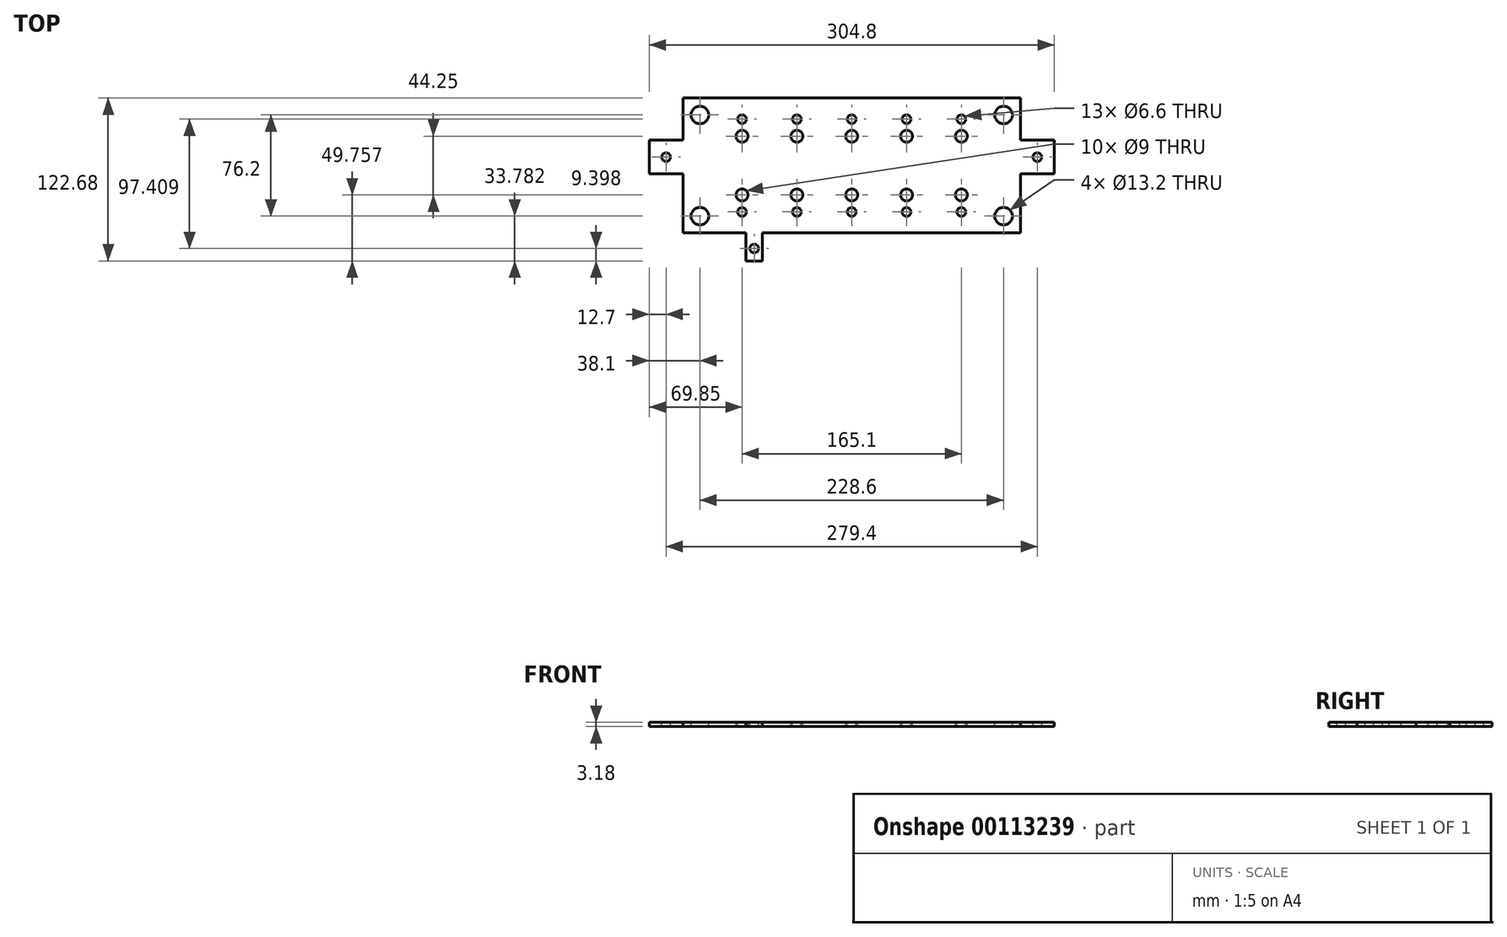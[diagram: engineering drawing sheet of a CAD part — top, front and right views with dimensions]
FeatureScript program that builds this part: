
annotation { "Feature Type Name" : "Feature", "Feature Type Description" : "" }
export const myFeature = defineFeature(function(context is Context, id is Id, definition is map)
    precondition{}
    {
        {
            var Q0;
            Q0=qCreatedBy(makeId("Top.planeOp"),FACE);
            var sketch = newSketch(context, id + "F0", { "sketchPlane" : qUnion([Q0])});
            skLineSegment(sketch, "E0.bottom", {"start": v(-102.08, 88.55) * mm, "end": v(177.32, 88.55) * mm});
            skLineSegment(sketch, "E0.top", {"start": v(-102.08, -13.05) * mm, "end": v(177.32, -13.05) * mm});
            skLineSegment(sketch, "E0.left", {"start": v(-102.08, 88.55) * mm, "end": v(-102.08, -13.05) * mm});
            skLineSegment(sketch, "E0.right", {"start": v(177.32, 88.55) * mm, "end": v(177.32, -13.05) * mm});
            skSolve(sketch);
        }
        {
            var Q0;
            Q0=makeQuery(id+"F0.imprint","IMPRINT",FACE,{"disambiguationData":[TD([[makeQuery(id+"F0.imprint","IMPRINT",EDGE,{"derivedFrom":sQuery(id+"F0.wireOp",EDGE,"E0.bottom")}),-1.0]])]});
            extrude(context, id + "F1", {"entities" : qUnion([Q0]), "depth" : 3.17 * mm});
        }
        {
            var Q0;
            Q0=makeQuery(id+"F1.opExtrude","CAP_FACE",FACE,{"disambiguationData":[OSD([sQuery(id+"F0.wireOp",EDGE,"E0.bottom"),sQuery(id+"F0.wireOp",EDGE,"E0.top"),sQuery(id+"F0.wireOp",EDGE,"E0.left"),sQuery(id+"F0.wireOp",EDGE,"E0.right")])],"isStart":false});
            var sketch = newSketch(context, id + "F2", { "sketchPlane" : qUnion([Q0])});
            skLineSegment(sketch, "E1", {"start": v(-102.08, 31.4) * mm, "end": v(-76.68, 31.4) * mm});
            skLineSegment(sketch, "E2", {"start": v(-76.68, 31.4) * mm, "end": v(-76.68, -13.05) * mm});
            skLineSegment(sketch, "E3", {"start": v(-102.08, 56.8) * mm, "end": v(-76.68, 56.8) * mm});
            skLineSegment(sketch, "E4", {"start": v(-76.68, 56.8) * mm, "end": v(-76.68, 88.55) * mm});
            skSolve(sketch);
        }
        {
            var Q0;
            {var subQ0=sQuery(id+"F2.wireOp",EDGE,"E1");Q0=makeQuery(id+"F2.imprint","IMPRINT",FACE,{"disambiguationData":[TD([[makeQuery(id+"F2.imprint","IMPRINT",EDGE,{"derivedFrom":subQ0}),-1.0]])]});}
            var Q1;
            {var subQ0=sQuery(id+"F2.wireOp",EDGE,"E3");Q1=makeQuery(id+"F2.imprint","IMPRINT",FACE,{"disambiguationData":[TD([[makeQuery(id+"F2.imprint","IMPRINT",EDGE,{"derivedFrom":subQ0}),1.0]])]});}
            extrude(context, id + "F3", {"entities" : qUnion([Q0, Q1]), "operationType" : NewBodyOperationType.REMOVE, "endBound" : BoundingType.THROUGH_ALL, "oppositeDirection" : true, "depth" : 25.4 * mm});
        }
        {
            var Q0;
            Q0=makeQuery(id+"F1.opExtrude","CAP_FACE",FACE,{"disambiguationData":[OSD([sQuery(id+"F0.wireOp",EDGE,"E0.bottom"),sQuery(id+"F0.wireOp",EDGE,"E0.top"),sQuery(id+"F0.wireOp",EDGE,"E0.left"),sQuery(id+"F0.wireOp",EDGE,"E0.right")])],"isStart":true});
            var sketch = newSketch(context, id + "F4", { "sketchPlane" : qUnion([Q0])});
            skLineSegment(sketch, "E5.bottom", {"start": v(-29.18, 13.05) * mm, "end": v(-17, 13.05) * mm});
            skLineSegment(sketch, "E5.top", {"start": v(-29.18, 34.13) * mm, "end": v(-17, 34.13) * mm});
            skLineSegment(sketch, "E5.left", {"start": v(-29.18, 13.05) * mm, "end": v(-29.18, 34.13) * mm});
            skLineSegment(sketch, "E5.right", {"start": v(-17, 13.05) * mm, "end": v(-17, 34.13) * mm});
            skSolve(sketch);
        }
        {
            var Q0;
            Q0=makeQuery(id+"F4.imprint","IMPRINT",FACE,{"disambiguationData":[TD([[makeQuery(id+"F4.imprint","IMPRINT",EDGE,{"derivedFrom":sQuery(id+"F4.wireOp",EDGE,"E5.bottom")}),1.0]])]});
            var Q1;
            {var subQ8=sQuery(id+"F4.wireOp",EDGE,"E5.bottom");Q1=makeQuery(id+"F4.imprint","IMPRINT",FACE,{"disambiguationData":[TD([[makeQuery(id+"F4.imprint","IMPRINT",EDGE,{"derivedFrom":subQ8}),-1.0]])]});}
            extrude(context, id + "F5", {"entities" : qUnion([Q0, Q1]), "operationType" : NewBodyOperationType.ADD, "oppositeDirection" : true, "depth" : 3.17 * mm});
        }
        {
            var Q0;
            {var subQ0=sQuery(id+"F0.wireOp",EDGE,"E0.right");var subQ1=sQuery(id+"F0.wireOp",EDGE,"E0.left");var subQ2=sQuery(id+"F0.wireOp",EDGE,"E0.top");var subQ3=sQuery(id+"F0.wireOp",EDGE,"E0.bottom");Q0=makeQuery(id+"F5.boolean.opBoolean","MERGE",FACE,{"derivedFrom":[makeQuery(id+"F1.opExtrude","CAP_FACE",FACE,{"disambiguationData":[OSD([subQ3,subQ2,subQ1,subQ0])],"isStart":false}),makeQuery(id+"F5.opExtrude","CAP_FACE",FACE,{"disambiguationData":[OSD([subQ3,subQ2,subQ1,subQ0,sQuery(id+"F2.wireOp",EDGE,"E1"),sQuery(id+"F2.wireOp",EDGE,"E2"),sQuery(id+"F4.wireOp",EDGE,"E5.top"),sQuery(id+"F4.wireOp",EDGE,"E5.left"),sQuery(id+"F4.wireOp",EDGE,"E5.right")])],"isStart":false})]});}
            var sketch = newSketch(context, id + "F6", { "sketchPlane" : qUnion([Q0])});
            skPoint(sketch, "E6", {"position": v(-89.38, 44.1) * mm});
            skSolve(sketch);
        }
        {
            var Q0;
            Q0=sQuery(id+"F6.wireOp",VERTEX,"E6");
            var Q1;
            Q1=makeQuery(id+"F1.opExtrude","SWEPT_BODY",BODY,{"disambiguationData":[OSD([sQuery(id+"F0.wireOp",EDGE,"E0.bottom"),sQuery(id+"F0.wireOp",EDGE,"E0.top"),sQuery(id+"F0.wireOp",EDGE,"E0.left"),sQuery(id+"F0.wireOp",EDGE,"E0.right")])]});
            hole(context, id + "F7", {"style" : HoleStyle.SIMPLE, "endStyle" : HoleEndStyle.THROUGH, "standardTappedOrClearance" : lookupTablePath({ "standard" : "ISO", "fit" : "Normal", "size" : "M6", "type" : "Clearance" }), "standardBlindInLast" : lookupTablePath({ "fit" : "Standard", "standard" : "ISO", "size" : "M6", "type" : "Clearance" }), "holeDiameter" : 6.6 * mm, "locations" : qUnion([Q0]), "scope" : qUnion([Q1]), "isTappedThrough" : true});
        }
        {
            var Q0;
            {var subQ0=sQuery(id+"F0.wireOp",EDGE,"E0.right");var subQ1=sQuery(id+"F0.wireOp",EDGE,"E0.left");var subQ2=sQuery(id+"F0.wireOp",EDGE,"E0.top");var subQ3=sQuery(id+"F0.wireOp",EDGE,"E0.bottom");Q0=makeQuery(id+"F5.boolean.opBoolean","MERGE",FACE,{"derivedFrom":[makeQuery(id+"F1.opExtrude","CAP_FACE",FACE,{"disambiguationData":[OSD([subQ3,subQ2,subQ1,subQ0])],"isStart":false}),makeQuery(id+"F5.opExtrude","CAP_FACE",FACE,{"disambiguationData":[OSD([subQ3,subQ2,subQ1,subQ0,sQuery(id+"F2.wireOp",EDGE,"E1"),sQuery(id+"F2.wireOp",EDGE,"E2"),sQuery(id+"F4.wireOp",EDGE,"E5.top"),sQuery(id+"F4.wireOp",EDGE,"E5.left"),sQuery(id+"F4.wireOp",EDGE,"E5.right")])],"isStart":false})]});}
            var sketch = newSketch(context, id + "F8", { "sketchPlane" : qUnion([Q0])});
            skPoint(sketch, "E7", {"position": v(-63.98, 75.85) * mm});
            skSolve(sketch);
        }
        {
            var Q0;
            Q0=sQuery(id+"F8.wireOp",VERTEX,"E7");
            var Q1;
            Q1=makeQuery(id+"F1.opExtrude","SWEPT_BODY",BODY,{"disambiguationData":[OSD([sQuery(id+"F0.wireOp",EDGE,"E0.bottom"),sQuery(id+"F0.wireOp",EDGE,"E0.top"),sQuery(id+"F0.wireOp",EDGE,"E0.left"),sQuery(id+"F0.wireOp",EDGE,"E0.right")])]});
            hole(context, id + "F9", {"style" : HoleStyle.SIMPLE, "endStyle" : HoleEndStyle.THROUGH, "standardTappedOrClearance" : lookupTablePath({ "standard" : "ISO", "fit" : "Normal", "size" : "M12", "type" : "Clearance" }), "standardBlindInLast" : lookupTablePath({ "fit" : "Standard", "standard" : "ISO", "size" : "M12", "type" : "Clearance" }), "holeDiameter" : 13.2 * mm, "locations" : qUnion([Q0]), "scope" : qUnion([Q1]), "isTappedThrough" : true});
        }
        {
            var Q0;
            {var subQ0=sQuery(id+"F0.wireOp",EDGE,"E0.right");var subQ1=sQuery(id+"F0.wireOp",EDGE,"E0.left");var subQ2=sQuery(id+"F0.wireOp",EDGE,"E0.top");var subQ3=sQuery(id+"F0.wireOp",EDGE,"E0.bottom");Q0=makeQuery(id+"F5.boolean.opBoolean","MERGE",FACE,{"derivedFrom":[makeQuery(id+"F1.opExtrude","CAP_FACE",FACE,{"disambiguationData":[OSD([subQ3,subQ2,subQ1,subQ0])],"isStart":false}),makeQuery(id+"F5.opExtrude","CAP_FACE",FACE,{"disambiguationData":[OSD([subQ3,subQ2,subQ1,subQ0,sQuery(id+"F2.wireOp",EDGE,"E1"),sQuery(id+"F2.wireOp",EDGE,"E2"),sQuery(id+"F4.wireOp",EDGE,"E5.top"),sQuery(id+"F4.wireOp",EDGE,"E5.left"),sQuery(id+"F4.wireOp",EDGE,"E5.right")])],"isStart":false})]});}
            var sketch = newSketch(context, id + "F10", { "sketchPlane" : qUnion([Q0])});
            skLineSegment(sketch, "E8", {"start": v(50.32, 88.55) * mm, "end": v(50.32, -13.05) * mm, "construction": true});
            skLineSegment(sketch, "E9", {"start": v(50.32, 37.75) * mm, "end": v(-76.68, 37.75) * mm, "construction": true});
            skLineSegment(sketch, "E10", {"start": v(50.32, 37.75) * mm, "end": v(177.32, 37.75) * mm, "construction": true});
            skCircle(sketch, "E11.0", {"center": v(-63.98, 75.85) * mm, "radius": 6.6 * mm, "construction": true});
            skCircle(sketch, "E12.MirrorC", {"center": v(-63.98, -0.35) * mm, "radius": 6.6 * mm, "construction": true});
            skCircle(sketch, "E13.MirrorC", {"center": v(164.62, 75.85) * mm, "radius": 6.6 * mm, "construction": true});
            skCircle(sketch, "E14.MirrorC", {"center": v(164.62, -0.35) * mm, "radius": 6.6 * mm, "construction": true});
            skSolve(sketch);
        }
        {
            var Q0;
            Q0=sQuery(id+"F10.wireOp",VERTEX,"E12.MirrorC.center");
            var Q1;
            Q1=sQuery(id+"F10.wireOp",VERTEX,"E14.MirrorC.center");
            var Q2;
            Q2=sQuery(id+"F10.wireOp",VERTEX,"E13.MirrorC.center");
            var Q3;
            Q3=makeQuery(id+"F1.opExtrude","SWEPT_BODY",BODY,{"disambiguationData":[OSD([sQuery(id+"F0.wireOp",EDGE,"E0.bottom"),sQuery(id+"F0.wireOp",EDGE,"E0.top"),sQuery(id+"F0.wireOp",EDGE,"E0.left"),sQuery(id+"F0.wireOp",EDGE,"E0.right")])]});
            hole(context, id + "F11", {"style" : HoleStyle.SIMPLE, "endStyle" : HoleEndStyle.THROUGH, "standardTappedOrClearance" : lookupTablePath({ "standard" : "ISO", "fit" : "Normal", "size" : "M12", "type" : "Clearance" }), "standardBlindInLast" : lookupTablePath({ "fit" : "Standard", "standard" : "ISO", "size" : "M12", "type" : "Clearance" }), "holeDiameter" : 13.2 * mm, "locations" : qUnion([Q0, Q1, Q2]), "scope" : qUnion([Q3]), "isTappedThrough" : true});
        }
        {
            var Q0;
            {var subQ0=sQuery(id+"F0.wireOp",EDGE,"E0.right");var subQ1=sQuery(id+"F0.wireOp",EDGE,"E0.left");var subQ2=sQuery(id+"F0.wireOp",EDGE,"E0.top");var subQ3=sQuery(id+"F0.wireOp",EDGE,"E0.bottom");Q0=makeQuery(id+"F5.boolean.opBoolean","MERGE",FACE,{"derivedFrom":[makeQuery(id+"F1.opExtrude","CAP_FACE",FACE,{"disambiguationData":[OSD([subQ3,subQ2,subQ1,subQ0])],"isStart":false}),makeQuery(id+"F5.opExtrude","CAP_FACE",FACE,{"disambiguationData":[OSD([subQ3,subQ2,subQ1,subQ0,sQuery(id+"F2.wireOp",EDGE,"E1"),sQuery(id+"F2.wireOp",EDGE,"E2"),sQuery(id+"F4.wireOp",EDGE,"E5.top"),sQuery(id+"F4.wireOp",EDGE,"E5.left"),sQuery(id+"F4.wireOp",EDGE,"E5.right")])],"isStart":false})]});}
            var sketch = newSketch(context, id + "F12", { "sketchPlane" : qUnion([Q0])});
            skPoint(sketch, "E15", {"position": v(-23.09, -24.73) * mm});
            skSolve(sketch);
        }
        {
            var Q0;
            Q0=sQuery(id+"F12.wireOp",VERTEX,"E15");
            var Q1;
            Q1=makeQuery(id+"F1.opExtrude","SWEPT_BODY",BODY,{"disambiguationData":[OSD([sQuery(id+"F0.wireOp",EDGE,"E0.bottom"),sQuery(id+"F0.wireOp",EDGE,"E0.top"),sQuery(id+"F0.wireOp",EDGE,"E0.left"),sQuery(id+"F0.wireOp",EDGE,"E0.right")])]});
            hole(context, id + "F13", {"style" : HoleStyle.SIMPLE, "endStyle" : HoleEndStyle.THROUGH, "standardTappedOrClearance" : lookupTablePath({ "standard" : "ISO", "fit" : "Normal", "size" : "M6", "type" : "Clearance" }), "standardBlindInLast" : lookupTablePath({ "fit" : "Standard", "standard" : "ISO", "size" : "M6", "type" : "Clearance" }), "holeDiameter" : 6.6 * mm, "locations" : qUnion([Q0]), "scope" : qUnion([Q1]), "isTappedThrough" : true});
        }
        {
            var Q0;
            Q0=makeQuery(id+"F1.opExtrude","SWEPT_FACE",FACE,{"disambiguationData":[OSD([sQuery(id+"F0.wireOp",EDGE,"E0.right")])]});
            var sketch = newSketch(context, id + "F14", { "sketchPlane" : qUnion([Q0])});
            skLineSegment(sketch, "E16.bottom", {"start": v(56.8, 0) * mm, "end": v(31.4, 0) * mm});
            skLineSegment(sketch, "E16.top", {"start": v(56.8, 3.18) * mm, "end": v(31.4, 3.18) * mm});
            skLineSegment(sketch, "E16.right", {"start": v(31.4, 0) * mm, "end": v(31.4, 3.18) * mm});
            skLineSegment(sketch, "E17", {"start": v(56.8, 3.18) * mm, "end": v(56.8, 0) * mm});
            skSolve(sketch);
        }
        {
            var Q0;
            Q0=makeQuery(id+"F14.imprint","IMPRINT",FACE,{"disambiguationData":[TD([[makeQuery(id+"F14.imprint","IMPRINT",EDGE,{"derivedFrom":sQuery(id+"F14.wireOp",EDGE,"E16.bottom")}),-1.0]])]});
            extrude(context, id + "F15", {"entities" : qUnion([Q0]), "operationType" : NewBodyOperationType.ADD, "depth" : 25.4 * mm});
        }
        {
            var Q0;
            {var subQ0=sQuery(id+"F0.wireOp",EDGE,"E0.right");var subQ1=sQuery(id+"F0.wireOp",EDGE,"E0.left");var subQ2=sQuery(id+"F0.wireOp",EDGE,"E0.top");var subQ3=sQuery(id+"F0.wireOp",EDGE,"E0.bottom");Q0=makeQuery(id+"F15.boolean.opBoolean","MERGE",FACE,{"derivedFrom":[makeQuery(id+"F5.boolean.opBoolean","MERGE",FACE,{"derivedFrom":[makeQuery(id+"F1.opExtrude","CAP_FACE",FACE,{"disambiguationData":[OSD([subQ3,subQ2,subQ1,subQ0])],"isStart":true}),makeQuery(id+"F5.opExtrude","CAP_FACE",FACE,{"disambiguationData":[OSD([subQ3,subQ2,subQ1,subQ0,sQuery(id+"F2.wireOp",EDGE,"E1"),sQuery(id+"F2.wireOp",EDGE,"E2"),sQuery(id+"F4.wireOp",EDGE,"E5.top"),sQuery(id+"F4.wireOp",EDGE,"E5.left"),sQuery(id+"F4.wireOp",EDGE,"E5.right")])],"isStart":true})]}),makeQuery(id+"F15.opExtrude","SWEPT_FACE",FACE,{"disambiguationData":[OSD([sQuery(id+"F14.wireOp",EDGE,"E16.bottom")])]})]});}
            var sketch = newSketch(context, id + "F16", { "sketchPlane" : qUnion([Q0])});
            skPoint(sketch, "E18", {"position": v(190.02, -44.1) * mm});
            skSolve(sketch);
        }
        {
            var Q0;
            Q0=sQuery(id+"F16.wireOp",VERTEX,"E18");
            var Q1;
            Q1=makeQuery(id+"F1.opExtrude","SWEPT_BODY",BODY,{"disambiguationData":[OSD([sQuery(id+"F0.wireOp",EDGE,"E0.bottom"),sQuery(id+"F0.wireOp",EDGE,"E0.top"),sQuery(id+"F0.wireOp",EDGE,"E0.left"),sQuery(id+"F0.wireOp",EDGE,"E0.right")])]});
            hole(context, id + "F17", {"style" : HoleStyle.SIMPLE, "endStyle" : HoleEndStyle.THROUGH, "standardTappedOrClearance" : lookupTablePath({ "standard" : "ISO", "fit" : "Normal", "size" : "M6", "type" : "Clearance" }), "standardBlindInLast" : lookupTablePath({ "fit" : "Standard", "standard" : "ISO", "size" : "M6", "type" : "Clearance" }), "holeDiameter" : 6.6 * mm, "locations" : qUnion([Q0]), "scope" : qUnion([Q1]), "isTappedThrough" : true});
        }
        {
            var Q0;
            {var subQ0=sQuery(id+"F0.wireOp",EDGE,"E0.right");var subQ1=sQuery(id+"F0.wireOp",EDGE,"E0.left");var subQ2=sQuery(id+"F0.wireOp",EDGE,"E0.top");var subQ3=sQuery(id+"F0.wireOp",EDGE,"E0.bottom");Q0=makeQuery(id+"F15.boolean.opBoolean","MERGE",FACE,{"derivedFrom":[makeQuery(id+"F5.boolean.opBoolean","MERGE",FACE,{"derivedFrom":[makeQuery(id+"F1.opExtrude","CAP_FACE",FACE,{"disambiguationData":[OSD([subQ3,subQ2,subQ1,subQ0])],"isStart":false}),makeQuery(id+"F5.opExtrude","CAP_FACE",FACE,{"disambiguationData":[OSD([subQ3,subQ2,subQ1,subQ0,sQuery(id+"F2.wireOp",EDGE,"E1"),sQuery(id+"F2.wireOp",EDGE,"E2"),sQuery(id+"F4.wireOp",EDGE,"E5.top"),sQuery(id+"F4.wireOp",EDGE,"E5.left"),sQuery(id+"F4.wireOp",EDGE,"E5.right")])],"isStart":false})]}),makeQuery(id+"F15.opExtrude","SWEPT_FACE",FACE,{"disambiguationData":[OSD([sQuery(id+"F14.wireOp",EDGE,"E16.top")])]})]});}
            var sketch = newSketch(context, id + "F18", { "sketchPlane" : qUnion([Q0])});
            skCircle(sketch, "E19.0", {"center": v(-63.98, 75.85) * mm, "radius": 6.6 * mm});
            skCircle(sketch, "E20.0", {"center": v(164.62, 75.85) * mm, "radius": 6.6 * mm});
            skLineSegment(sketch, "E21", {"start": v(-76.68, 72.68) * mm, "end": v(-32.23, 72.68) * mm, "construction": true});
            skLineSegment(sketch, "E22", {"start": v(-32.23, 72.68) * mm, "end": v(9.04, 72.68) * mm, "construction": true});
            skLineSegment(sketch, "E23", {"start": v(9.04, 72.68) * mm, "end": v(50.32, 72.68) * mm, "construction": true});
            skLineSegment(sketch, "E24", {"start": v(50.32, 72.68) * mm, "end": v(91.6, 72.68) * mm, "construction": true});
            skLineSegment(sketch, "E25", {"start": v(91.6, 72.68) * mm, "end": v(132.87, 72.68) * mm, "construction": true});
            skLineSegment(sketch, "E26", {"start": v(132.87, 72.68) * mm, "end": v(177.32, 72.68) * mm, "construction": true});
            skPoint(sketch, "E27", {"position": v(-32.23, 72.68) * mm});
            skPoint(sketch, "E28", {"position": v(9.04, 72.68) * mm});
            skPoint(sketch, "E29", {"position": v(50.32, 72.68) * mm});
            skPoint(sketch, "E30", {"position": v(91.6, 72.68) * mm});
            skPoint(sketch, "E31", {"position": v(132.87, 72.68) * mm});
            skPoint(sketch, "E32", {"position": v(-32.23, 59.88) * mm});
            skPoint(sketch, "E33", {"position": v(9.04, 59.88) * mm});
            skPoint(sketch, "E34", {"position": v(50.32, 59.88) * mm});
            skPoint(sketch, "E35", {"position": v(91.6, 59.88) * mm});
            skPoint(sketch, "E36", {"position": v(132.87, 59.88) * mm});
            skPoint(sketch, "E37", {"position": v(-32.23, 15.63) * mm});
            skPoint(sketch, "E38", {"position": v(9.04, 15.63) * mm});
            skPoint(sketch, "E39", {"position": v(50.32, 15.63) * mm});
            skPoint(sketch, "E40", {"position": v(91.6, 15.63) * mm});
            skPoint(sketch, "E41", {"position": v(132.87, 15.63) * mm});
            skPoint(sketch, "E42", {"position": v(-32.23, 2.83) * mm});
            skPoint(sketch, "E43", {"position": v(9.04, 2.83) * mm});
            skPoint(sketch, "E44", {"position": v(50.32, 2.83) * mm});
            skPoint(sketch, "E45", {"position": v(91.6, 2.83) * mm});
            skPoint(sketch, "E46", {"position": v(132.87, 2.83) * mm});
            skLineSegment(sketch, "E47", {"start": v(-32.23, 2.83) * mm, "end": v(-32.23, 15.63) * mm, "construction": true});
            skLineSegment(sketch, "E48", {"start": v(-32.23, 59.88) * mm, "end": v(-32.23, 72.68) * mm, "construction": true});
            skLineSegment(sketch, "E49", {"start": v(50.32, 72.68) * mm, "end": v(50.32, 88.55) * mm, "construction": true});
            skLineSegment(sketch, "E50", {"start": v(50.32, 2.83) * mm, "end": v(50.32, -13.05) * mm, "construction": true});
            skSolve(sketch);
        }
        {
            var Q0;
            Q0=sQuery(id+"F18.wireOp",VERTEX,"E32");
            var Q1;
            Q1=sQuery(id+"F18.wireOp",VERTEX,"E33");
            var Q2;
            Q2=sQuery(id+"F18.wireOp",VERTEX,"E34");
            var Q3;
            Q3=sQuery(id+"F18.wireOp",VERTEX,"E35");
            var Q4;
            Q4=sQuery(id+"F18.wireOp",VERTEX,"E36");
            var Q5;
            Q5=sQuery(id+"F18.wireOp",VERTEX,"E41");
            var Q6;
            Q6=sQuery(id+"F18.wireOp",VERTEX,"E40");
            var Q7;
            Q7=sQuery(id+"F18.wireOp",VERTEX,"E39");
            var Q8;
            Q8=sQuery(id+"F18.wireOp",VERTEX,"E38");
            var Q9;
            Q9=sQuery(id+"F18.wireOp",VERTEX,"E37");
            var Q10;
            Q10=makeQuery(id+"F1.opExtrude","SWEPT_BODY",BODY,{"disambiguationData":[OSD([sQuery(id+"F0.wireOp",EDGE,"E0.bottom"),sQuery(id+"F0.wireOp",EDGE,"E0.top"),sQuery(id+"F0.wireOp",EDGE,"E0.left"),sQuery(id+"F0.wireOp",EDGE,"E0.right")])]});
            hole(context, id + "F19", {"style" : HoleStyle.SIMPLE, "endStyle" : HoleEndStyle.THROUGH, "holeDiameter" : 9 * mm, "locations" : qUnion([Q0, Q1, Q2, Q3, Q4, Q5, Q6, Q7, Q8, Q9]), "scope" : qUnion([Q10]), "isTappedThrough" : true});
        }
        {
            var Q0;
            Q0=sQuery(id+"F18.wireOp",VERTEX,"E27");
            var Q1;
            Q1=sQuery(id+"F18.wireOp",VERTEX,"E42");
            var Q2;
            Q2=sQuery(id+"F18.wireOp",VERTEX,"E43");
            var Q3;
            Q3=sQuery(id+"F18.wireOp",VERTEX,"E28");
            var Q4;
            Q4=sQuery(id+"F18.wireOp",VERTEX,"E29");
            var Q5;
            Q5=sQuery(id+"F18.wireOp",VERTEX,"E44");
            var Q6;
            Q6=sQuery(id+"F18.wireOp",VERTEX,"E45");
            var Q7;
            Q7=sQuery(id+"F18.wireOp",VERTEX,"E30");
            var Q8;
            Q8=sQuery(id+"F18.wireOp",VERTEX,"E31");
            var Q9;
            Q9=sQuery(id+"F18.wireOp",VERTEX,"E46");
            var Q10;
            Q10=makeQuery(id+"F1.opExtrude","SWEPT_BODY",BODY,{"disambiguationData":[OSD([sQuery(id+"F0.wireOp",EDGE,"E0.bottom"),sQuery(id+"F0.wireOp",EDGE,"E0.top"),sQuery(id+"F0.wireOp",EDGE,"E0.left"),sQuery(id+"F0.wireOp",EDGE,"E0.right")])]});
            hole(context, id + "F20", {"style" : HoleStyle.SIMPLE, "endStyle" : HoleEndStyle.THROUGH, "standardTappedOrClearance" : lookupTablePath({ "standard" : "ISO", "fit" : "Normal", "size" : "M6", "type" : "Clearance" }), "standardBlindInLast" : lookupTablePath({ "fit" : "Standard", "standard" : "ISO", "size" : "M6", "type" : "Clearance" }), "holeDiameter" : 6.6 * mm, "locations" : qUnion([Q0, Q1, Q2, Q3, Q4, Q5, Q6, Q7, Q8, Q9]), "scope" : qUnion([Q10]), "isTappedThrough" : true});
        }
    });
